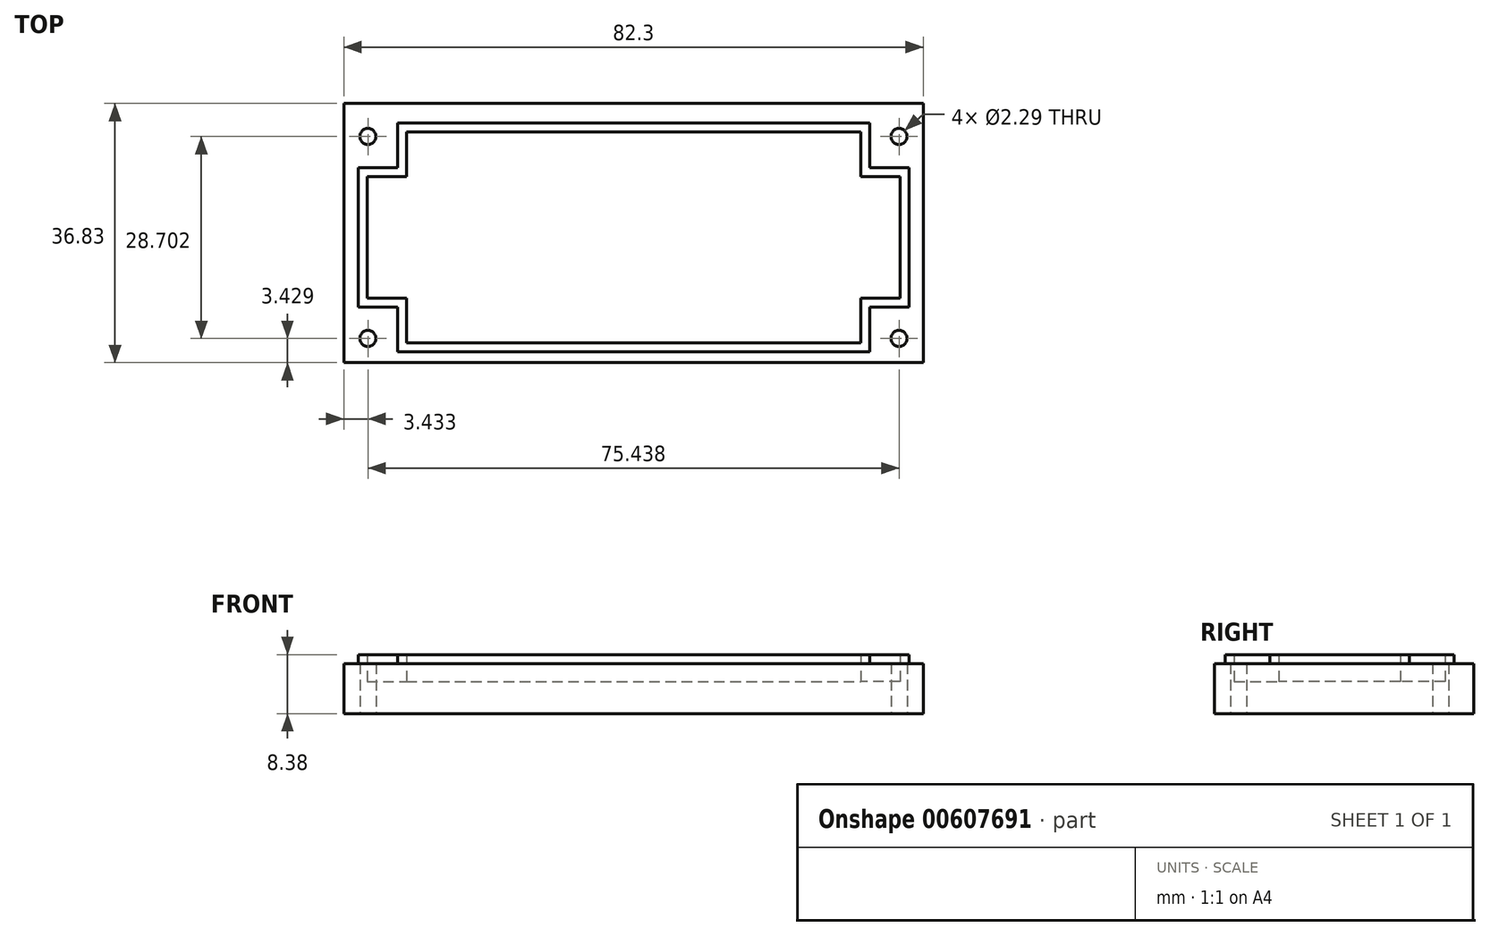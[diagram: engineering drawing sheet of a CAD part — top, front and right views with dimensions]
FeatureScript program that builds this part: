
annotation { "Feature Type Name" : "Feature", "Feature Type Description" : "" }
export const myFeature = defineFeature(function(context is Context, id is Id, definition is map)
    precondition{}
    {
        {
            var Q0;
            Q0=qCreatedBy(makeId("Top.planeOp"),FACE);
            var sketch = newSketch(context, id + "F0", { "sketchPlane" : qUnion([Q0])});
            skLineSegment(sketch, "E0", {"start": v(0, 0) * mm, "end": v(0, 36.83) * mm});
            skLineSegment(sketch, "E1", {"start": v(0, 36.83) * mm, "end": v(-82.3, 36.83) * mm});
            skLineSegment(sketch, "E2", {"start": v(-82.3, 36.83) * mm, "end": v(-82.3, 0) * mm});
            skLineSegment(sketch, "E3", {"start": v(-82.3, 0) * mm, "end": v(0, 0) * mm});
            skLineSegment(sketch, "E4", {"start": v(-7.62, 1.52) * mm, "end": v(-7.62, 7.87) * mm});
            skLineSegment(sketch, "E5", {"start": v(-7.62, 7.87) * mm, "end": v(-2.03, 7.87) * mm});
            skLineSegment(sketch, "E6", {"start": v(-2.03, 7.87) * mm, "end": v(-2.03, 27.69) * mm});
            skLineSegment(sketch, "E7", {"start": v(-2.03, 27.69) * mm, "end": v(-7.62, 27.69) * mm});
            skLineSegment(sketch, "E8", {"start": v(-7.62, 27.69) * mm, "end": v(-7.62, 34.04) * mm});
            skLineSegment(sketch, "E9", {"start": v(-7.62, 34.04) * mm, "end": v(-74.68, 34.04) * mm});
            skLineSegment(sketch, "E10", {"start": v(-74.68, 34.04) * mm, "end": v(-74.68, 27.69) * mm});
            skLineSegment(sketch, "E11", {"start": v(-74.68, 27.69) * mm, "end": v(-80.26, 27.69) * mm});
            skLineSegment(sketch, "E12", {"start": v(-80.26, 27.69) * mm, "end": v(-80.26, 7.87) * mm});
            skLineSegment(sketch, "E13", {"start": v(-80.26, 7.87) * mm, "end": v(-74.68, 7.87) * mm});
            skLineSegment(sketch, "E14", {"start": v(-74.68, 7.87) * mm, "end": v(-74.68, 1.52) * mm});
            skLineSegment(sketch, "E15", {"start": v(-74.68, 1.52) * mm, "end": v(-7.62, 1.52) * mm});
            skLineSegment(sketch, "E16", {"start": v(-8.89, 2.8) * mm, "end": v(-8.89, 9.14) * mm});
            skLineSegment(sketch, "E17", {"start": v(-8.9, 9.14) * mm, "end": v(-3.3, 9.14) * mm});
            skLineSegment(sketch, "E18", {"start": v(-3.3, 9.14) * mm, "end": v(-3.3, 26.42) * mm});
            skLineSegment(sketch, "E19", {"start": v(-3.3, 26.42) * mm, "end": v(-8.9, 26.42) * mm});
            skLineSegment(sketch, "E20", {"start": v(-8.9, 26.42) * mm, "end": v(-8.9, 32.77) * mm});
            skLineSegment(sketch, "E21", {"start": v(-8.9, 32.77) * mm, "end": v(-73.4, 32.77) * mm});
            skLineSegment(sketch, "E22", {"start": v(-73.4, 32.77) * mm, "end": v(-73.4, 26.42) * mm});
            skLineSegment(sketch, "E23", {"start": v(-73.4, 26.42) * mm, "end": v(-79, 26.42) * mm});
            skLineSegment(sketch, "E24", {"start": v(-79, 26.42) * mm, "end": v(-79, 9.14) * mm});
            skLineSegment(sketch, "E25", {"start": v(-79, 9.14) * mm, "end": v(-73.4, 9.14) * mm});
            skLineSegment(sketch, "E26", {"start": v(-73.4, 9.14) * mm, "end": v(-73.4, 2.8) * mm});
            skLineSegment(sketch, "E27", {"start": v(-73.4, 2.8) * mm, "end": v(-8.89, 2.8) * mm});
            skCircle(sketch, "E28", {"center": v(-3.43, 3.43) * mm, "radius": 1.14 * mm});
            skLineSegment(sketch, "E29", {"start": v(-3.3, 17.78) * mm, "end": v(-79, 17.78) * mm, "construction": true});
            skCircle(sketch, "E30.MirrorC", {"center": v(-3.43, 32.13) * mm, "radius": 1.14 * mm});
            skLineSegment(sketch, "E31", {"start": v(-41.15, 32.77) * mm, "end": v(-41.15, 2.8) * mm, "construction": true});
            skCircle(sketch, "E32.MirrorC", {"center": v(-78.87, 32.13) * mm, "radius": 1.14 * mm});
            skCircle(sketch, "E33.MirrorC", {"center": v(-78.87, 3.43) * mm, "radius": 1.14 * mm});
            skSolve(sketch);
        }
        {
            var Q0;
            Q0=makeQuery(id+"F0.imprint","IMPRINT",FACE,{"disambiguationData":[TD([[makeQuery(id+"F0.imprint","IMPRINT",EDGE,{"derivedFrom":sQuery(id+"F0.wireOp",EDGE,"E0")}),1.0]])]});
            extrude(context, id + "F1", {"entities" : qUnion([Q0]), "depth" : 7.11 * mm, "offsetDistance" : 25.4 * mm});
        }
        {
            var Q0;
            Q0=makeQuery(id+"F0.imprint","IMPRINT",FACE,{"disambiguationData":[TD([[makeQuery(id+"F0.imprint","IMPRINT",EDGE,{"derivedFrom":sQuery(id+"F0.wireOp",EDGE,"E4")}),1.0]])]});
            extrude(context, id + "F2", {"entities" : qUnion([Q0]), "operationType" : NewBodyOperationType.ADD, "depth" : 8.38 * mm, "offsetDistance" : 25.4 * mm});
        }
        {
            var Q0;
            Q0=makeQuery(id+"F0.imprint","IMPRINT",FACE,{"disambiguationData":[TD([[makeQuery(id+"F0.imprint","IMPRINT",EDGE,{"derivedFrom":sQuery(id+"F0.wireOp",EDGE,"E16")}),1.0]])]});
            extrude(context, id + "F3", {"entities" : qUnion([Q0]), "operationType" : NewBodyOperationType.ADD, "depth" : 4.57 * mm, "offsetDistance" : 25.4 * mm});
        }
    });
